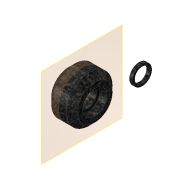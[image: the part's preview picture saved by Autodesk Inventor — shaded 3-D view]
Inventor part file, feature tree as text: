
AUTODESK INVENTOR PART (.ipt)
format: ipt  version: 2019.4 (Build 234330000, 330)  size: 160,768 bytes
history: native  units: mm
features: sketch x4, revolve x2, extrude x2, plane x1, projected_geometry x1
ambient origin geometry x8: Origin, YZ Plane, XZ Plane, XY Plane, X Axis, Y Axis, Z Axis, Center Point
bodies: Solid1 (feature_tree)
feature tree (10):
  revolve  "Revolution1"  [1 undecoded]
  plane  "Work Plane1"
  extrude  "Extrusion1"  TaperAngle=90.0deg  [1 undecoded]
  revolve  "Revolution2"  Angle=45.0deg
  extrude  "Extrusion2"  Depth=1.0mm
  sketch  "Sketch1"  dims[d0=8.8mm d1=7.75mm]
  sketch  "Sketch2"  dims[d3=1.9mm d6=90.0deg]
  sketch  "Sketch3"  dims[d8=5.0mm d9=45.0deg]
  projected_geometry  "Projected Loop1"
  sketch  "Sketch4"  dims[d10=135.0deg d11=5.1mm d12=10.0mm d13=0.0mm d14=2.5mm d15=4.1mm d16=2.5mm d17=90.0deg d18=5.0mm d19=6.5mm d20=1.0mm d21=0.0mm]
note: 2 required parameter values undecoded (feature->parameter linkage not recoverable at this tier; creation-order binding heuristic only, values carry confidence <= 0.55)